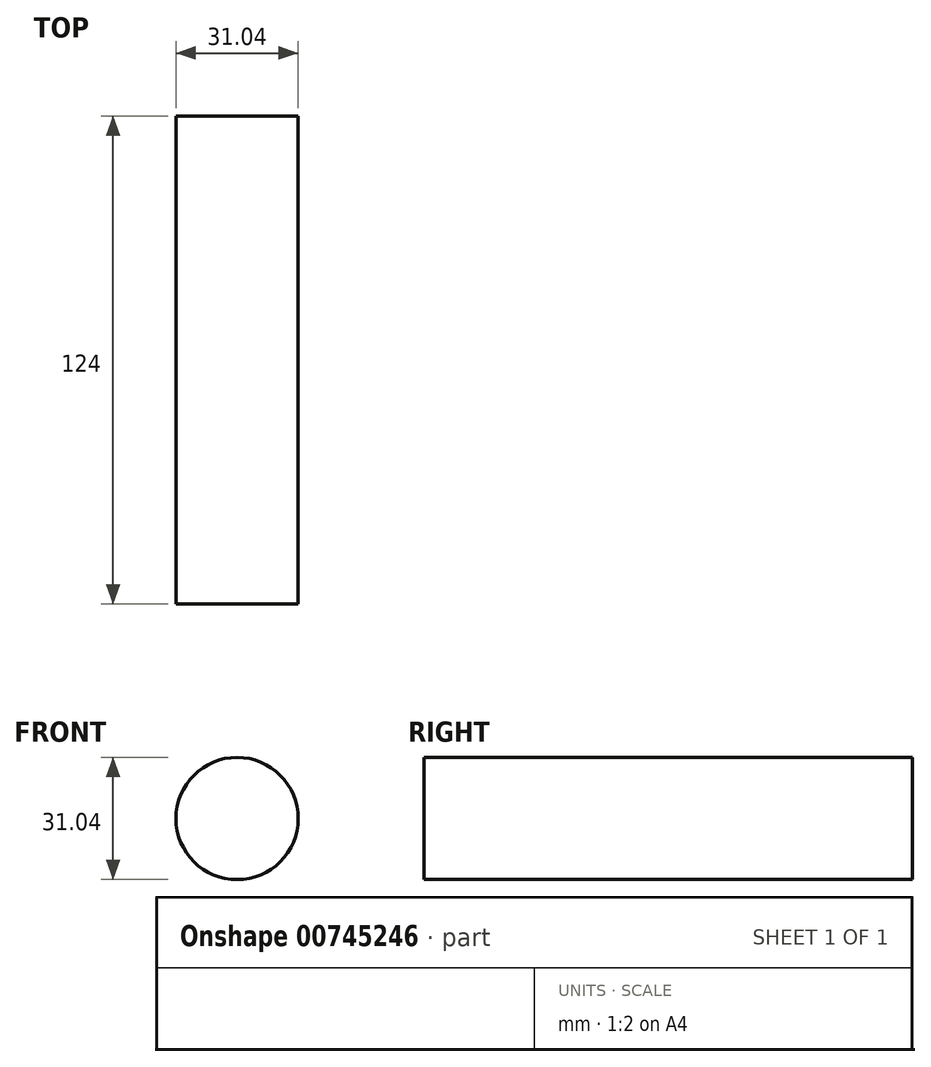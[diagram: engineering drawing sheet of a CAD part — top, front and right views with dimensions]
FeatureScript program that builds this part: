
annotation { "Feature Type Name" : "Feature", "Feature Type Description" : "" }
export const myFeature = defineFeature(function(context is Context, id is Id, definition is map)
    precondition{}
    {
        {
            var Q0;
            Q0=qCreatedBy(makeId("Front.planeOp"),FACE);
            var sketch = newSketch(context, id + "F0", { "sketchPlane" : qUnion([Q0])});
            skCircle(sketch, "E0", {"center": v(-1.7, 0) * mm, "radius": 15.52 * mm});
            skSolve(sketch);
        }
        {
            var Q0;
            Q0 = qSketchRegion(id + "F0", true);
            extrude(context, id + "F1", {"entities" : qUnion([Q0]), "depth" : 124 * mm, "offsetDistance" : 25 * mm});
        }
    });
